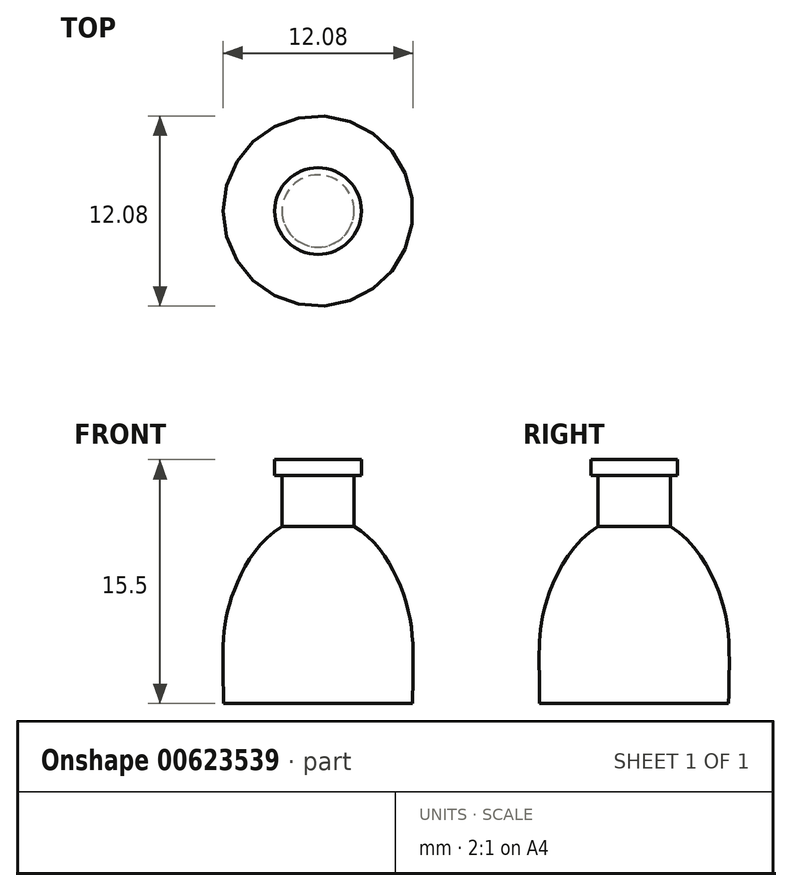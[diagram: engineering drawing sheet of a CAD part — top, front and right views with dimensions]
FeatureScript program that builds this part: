
annotation { "Feature Type Name" : "Feature", "Feature Type Description" : "" }
export const myFeature = defineFeature(function(context is Context, id is Id, definition is map)
    precondition{}
    {
        {
            var Q0;
            Q0=qCreatedBy(makeId("Front.planeOp"),FACE);
            var sketch = newSketch(context, id + "F0", { "sketchPlane" : qUnion([Q0])});
            skLineSegment(sketch, "E0", {"start": v(0, 0) * mm, "end": v(-6, 0) * mm});
            skLineSegment(sketch, "E1", {"start": v(0, 0) * mm, "end": v(0, 12) * mm});
            skFitSpline(sketch, "E2", {"points": [v(0, 12) * mm, v(-5.48, 6.76) * mm, v(-6, 0) * mm], "startDerivative": vector(-18.84, -1.7) * mm, "endDerivative": vector(0.32, -21.07) * mm});
            skSolve(sketch);
        }
        {
            var Q0;
            Q0 = qSketchRegion(id + "F0", true);
            var Q1;
            Q1=sQuery(id+"F0.wireOp",EDGE,"E1");
            revolve(context, id + "F1", {"entities" : qUnion([Q0]), "axis" : qUnion([Q1]), "revolveType" : RevolveType.FULL});
        }
        {
            var Q0;
            Q0=qCreatedBy(makeId("Top.planeOp"),FACE);
            cPlane(context, id + "F2", {"entities" : qUnion([Q0]), "cplaneType" : CPlaneType.OFFSET, "offset" : 12 * mm, "width" : 152.4 * mm, "height" : 152.4 * mm});
        }
        {
            var Q0;
            Q0=qCreatedBy(id+"F2.planeOp",FACE);
            var sketch = newSketch(context, id + "F3", { "sketchPlane" : qUnion([Q0])});
            skCircle(sketch, "E3", {"center": v(0, 0) * mm, "radius": 2.3 * mm});
            skSolve(sketch);
        }
        {
            var Q0;
            Q0 = qSketchRegion(id + "F3", true);
            extrude(context, id + "F4", {"entities" : qUnion([Q0]), "operationType" : NewBodyOperationType.ADD, "endBound" : BoundingType.SYMMETRIC, "depth" : 5 * mm, "offsetDistance" : 25.4 * mm});
        }
        {
            var Q0;
            Q0=makeQuery(id+"F4.opExtrude","CAP_FACE",FACE,{"disambiguationData":[OSD([sQuery(id+"F3.wireOp",EDGE,"E3")])],"isStart":false});
            var sketch = newSketch(context, id + "F5", { "sketchPlane" : qUnion([Q0])});
            skCircle(sketch, "E4", {"center": v(0, 0) * mm, "radius": 2.75 * mm});
            skSolve(sketch);
        }
        {
            var Q0;
            Q0 = qSketchRegion(id + "F5", true);
            extrude(context, id + "F6", {"entities" : qUnion([Q0]), "operationType" : NewBodyOperationType.ADD, "depth" : 1 * mm, "offsetDistance" : 25.4 * mm});
        }
    });
